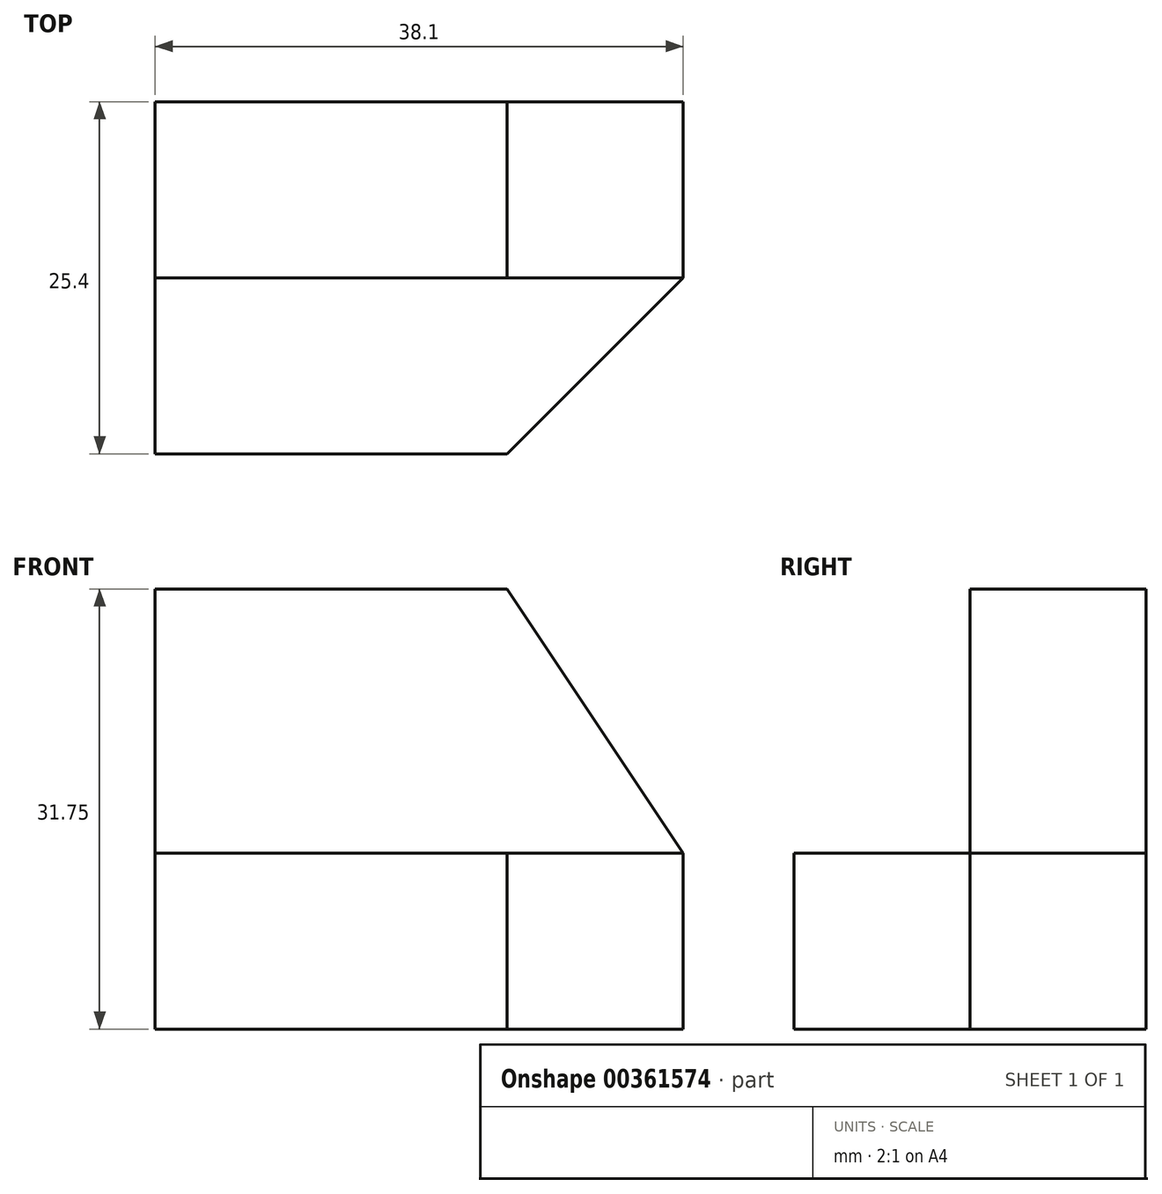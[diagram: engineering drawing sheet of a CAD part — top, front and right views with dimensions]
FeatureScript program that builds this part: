
annotation { "Feature Type Name" : "Feature", "Feature Type Description" : "" }
export const myFeature = defineFeature(function(context is Context, id is Id, definition is map)
    precondition{}
    {
        {
            var Q0;
            Q0=qCreatedBy(makeId("Front.planeOp"),FACE);
            var sketch = newSketch(context, id + "F0", { "sketchPlane" : qUnion([Q0])});
            skLineSegment(sketch, "E0", {"start": v(0, 0) * mm, "end": v(38.1, 0) * mm});
            skLineSegment(sketch, "E1", {"start": v(38.1, 0) * mm, "end": v(38.1, 31.75) * mm});
            skLineSegment(sketch, "E2", {"start": v(38.1, 31.75) * mm, "end": v(0, 31.75) * mm});
            skLineSegment(sketch, "E3", {"start": v(0, 31.75) * mm, "end": v(0, 0) * mm});
            skSolve(sketch);
        }
        {
            var Q0;
            Q0=makeQuery(id+"F0.imprint","IMPRINT",FACE,{"disambiguationData":[TD([[makeQuery(id+"F0.imprint","IMPRINT",EDGE,{"derivedFrom":sQuery(id+"F0.wireOp",EDGE,"E0")}),1.0]])]});
            extrude(context, id + "F1", {"entities" : qUnion([Q0]), "depth" : 25.4 * mm});
        }
        {
            var Q0;
            Q0=makeQuery(id+"F1.opExtrude","CAP_FACE",FACE,{"disambiguationData":[OSD([sQuery(id+"F0.wireOp",EDGE,"E0"),sQuery(id+"F0.wireOp",EDGE,"E1"),sQuery(id+"F0.wireOp",EDGE,"E2"),sQuery(id+"F0.wireOp",EDGE,"E3")])],"isStart":true});
            var sketch = newSketch(context, id + "F2", { "sketchPlane" : qUnion([Q0])});
            skLineSegment(sketch, "E4", {"start": v(-25.4, 31.75) * mm, "end": v(-38.1, 12.7) * mm});
            skSolve(sketch);
        }
        {
            var Q0;
            {var subQ0=sQuery(id+"F2.wireOp",EDGE,"E4");Q0=makeQuery(id+"F2.imprint","IMPRINT",FACE,{"disambiguationData":[TD([[makeQuery(id+"F2.imprint","IMPRINT",EDGE,{"derivedFrom":subQ0}),-1.0]])]});}
            extrude(context, id + "F3", {"entities" : qUnion([Q0]), "operationType" : NewBodyOperationType.REMOVE, "oppositeDirection" : true, "depth" : 12.7 * mm});
        }
        {
            var Q0;
            Q0=makeQuery(id+"F1.opExtrude","SWEPT_FACE",FACE,{"disambiguationData":[OSD([sQuery(id+"F0.wireOp",EDGE,"E3")])]});
            var sketch = newSketch(context, id + "F4", { "sketchPlane" : qUnion([Q0])});
            skLineSegment(sketch, "E5", {"start": v(12.7, 31.75) * mm, "end": v(12.7, 12.7) * mm});
            skPoint(sketch, "E5.endSnap0", {"position": v(12.7, 31.75) * mm});
            skLineSegment(sketch, "E6", {"start": v(12.7, 12.7) * mm, "end": v(25.4, 12.7) * mm});
            skSolve(sketch);
        }
        {
            var Q0;
            {var subQ0=sQuery(id+"F4.wireOp",EDGE,"E5");Q0=makeQuery(id+"F4.imprint","IMPRINT",FACE,{"disambiguationData":[TD([[makeQuery(id+"F4.imprint","IMPRINT",EDGE,{"derivedFrom":subQ0}),1.0]])]});}
            extrude(context, id + "F5", {"entities" : qUnion([Q0]), "operationType" : NewBodyOperationType.REMOVE, "oppositeDirection" : true, "depth" : 38.1 * mm});
        }
        {
            var Q0;
            Q0=makeQuery(id+"F5.boolean.opBoolean","COPY",FACE,{"derivedFrom":makeQuery(id+"F5.opExtrude","SWEPT_FACE",FACE,{"disambiguationData":[OSD([sQuery(id+"F4.wireOp",EDGE,"E6")])]})});
            var sketch = newSketch(context, id + "F6", { "sketchPlane" : qUnion([Q0])});
            skLineSegment(sketch, "E7", {"start": v(38.1, -12.7) * mm, "end": v(25.4, -25.4) * mm});
            skSolve(sketch);
        }
        {
            var Q0;
            {var subQ0=sQuery(id+"F6.wireOp",EDGE,"E7");Q0=makeQuery(id+"F6.imprint","IMPRINT",FACE,{"disambiguationData":[TD([[makeQuery(id+"F6.imprint","IMPRINT",EDGE,{"derivedFrom":subQ0}),1.0]])]});}
            extrude(context, id + "F7", {"entities" : qUnion([Q0]), "operationType" : NewBodyOperationType.REMOVE, "oppositeDirection" : true, "depth" : 12.7 * mm});
        }
    });
